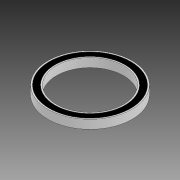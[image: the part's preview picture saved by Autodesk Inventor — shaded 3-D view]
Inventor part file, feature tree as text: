
AUTODESK INVENTOR PART (.ipt)
format: ipt  version: 2020 (Build 240168000, 168)  size: 125,952 bytes
history: native  units: mm
features: revolve x1, sketch x1
ambient origin geometry x8: Origin, YZ Plane, XZ Plane, XY Plane, X Axis, Y Axis, Z Axis, Center Point
bodies: Solid1 (feature_tree)
feature tree (2):
  revolve  "Revolution1"  [1 undecoded]
  sketch  "Sketch1"  dims[d0=50.0mm d2=13.0mm d5=62.5mm d6=0.2mm d7=2.0mm d8=90.0deg]
note: 1 required parameter value undecoded (feature->parameter linkage not recoverable at this tier; creation-order binding heuristic only, values carry confidence <= 0.55)
